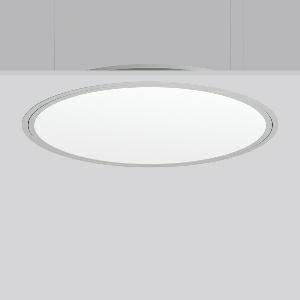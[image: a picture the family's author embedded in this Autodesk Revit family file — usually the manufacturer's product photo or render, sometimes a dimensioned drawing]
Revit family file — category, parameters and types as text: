
# Revit family: triona_round_e_312387_004_1_12_2095
name_source: partatom
category: Lighting Fixtures
units: mm (PartAtom-declared; Revit-internal decimal feet)

## family parameters
Cut with Voids When Loaded = No
Host = Face
Light Source = No
Part Type = Normal
Room Calculation Point = No
Round Connector Dimension = Use Diameter
Shared = No

## types (1)
- TRIONA round E (1 x LED Modul 840, 8300 lm, 4000)
    Apparent Load = 80 VA
    CIE Flux Codes = 49 80 96 100 100
    Color Rendering = 80
    Color Temperature = 4000
    Default Elevation = 1800 mm
    Description = Series: TRIONA round
Decorative round LED recessed surface luminaire. Cover made of sheet steel, powder-coated. Frame made of aluminium, powder-coated. Recessed ring: aluminium extrusion profile, powder coated. Light emission through a diffuser: plastic, opal. Lightguide and diffuser made of non-yellowing plastic (PMMA). Lateral light emission (RZB SIDELITE technology) for above-average homogeneous light distribution. Suitable for installation in cavity ceilings. Tool-free mounting system thanks to the rocker arm mechanism (patent pending). Electronic ballast included. Very easy installation thanks to Plug+Play connection. 
Colour: silver, matt (approx. RAL 9006)
Diameter: 889 mm
Height: 2 mm
Cut-out diameter: 866 mm
Recess height: 100 mm
Luminaire: recess height: 89 mm
Lamp: LED
Socket: without socket
Colour temperature: 4000K
Colour rendering index (CRI): 80
System power: 80 W
Rated luminous flux: 8300 lm
Luminous efficiency: 104 lm/W
Control gear: Converter, dimmable, DALI
Protection class: I
Type of protection: IP 40
    Height = 0 mm  [stored 0 ft]
    Lamp = 1 x LED Modul 840
    Lamp Light Flux = 8300 lm
    Lamp count = 1
    Length = 889 mm
    Lifetime = 50000 h
    Luminous efficacy = 104 lm/W
    Manufacturer = RZB
    ModVariant = No
    Model = 312387.004.1.12
    Mounting Place = Ceiling
    Mounting Type = Recessed
    Number of Poles = 1
    OnlyDefault = Yes
    Power Factor = 1
    Product Name = TRIONA round E
    Product group = Recessed modular luminaires
    ProductGroupID = 406
    Protection Class = Protection class I
    Protection Degree = IP 20
    RLX_Detail_Level = 1
    RLX_Emergency_Light_Flux = 0 lm
    RLX_Emergency_Type = 0
    RLX_Emergency_Type_DB = No
    RlxData = <blob elided: 38817 chars, md5=e872a67a>
    Socket = socket
    Standby Power = 0 W
    System Light Flux = 8300 lm
    System Power = 80 W
    Type Comments = Product without accessories
    Type Image = 312387.004.12.jpg
    URL = http://relux.com
    VarID = ---
    Voltage = 230 V
    Voltage Range = 220-240 V
    Weight = 0.00 kg
    Width = 0 mm  [stored 0 ft]

note: [stored X ft] marks values corroborated as IEEE doubles in the binary element streams (Revit-internal decimal feet)

## geometry (parser evidence)
native form markers: Blend x4, Sweep x9
no freeform markers — native parametric forms only
